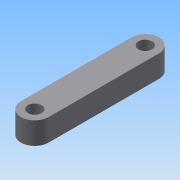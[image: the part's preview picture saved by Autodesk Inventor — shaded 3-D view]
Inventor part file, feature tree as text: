
AUTODESK INVENTOR PART (.ipt)
format: ipt  version: 2015 (Build 190159000, 159)  size: 79,360 bytes
history: native  units: mm
features: other x1, extrude x1, sketch x1
ambient origin geometry x8: Origin, YZ Plane, XZ Plane, XY Plane, X Axis, Y Axis, Z Axis, Center Point
bodies: Body1 (feature_tree)
feature tree (3):
  other  "實體1"
  extrude  "擠出1"  Depth=10.0mm
  sketch  "草圖1"
